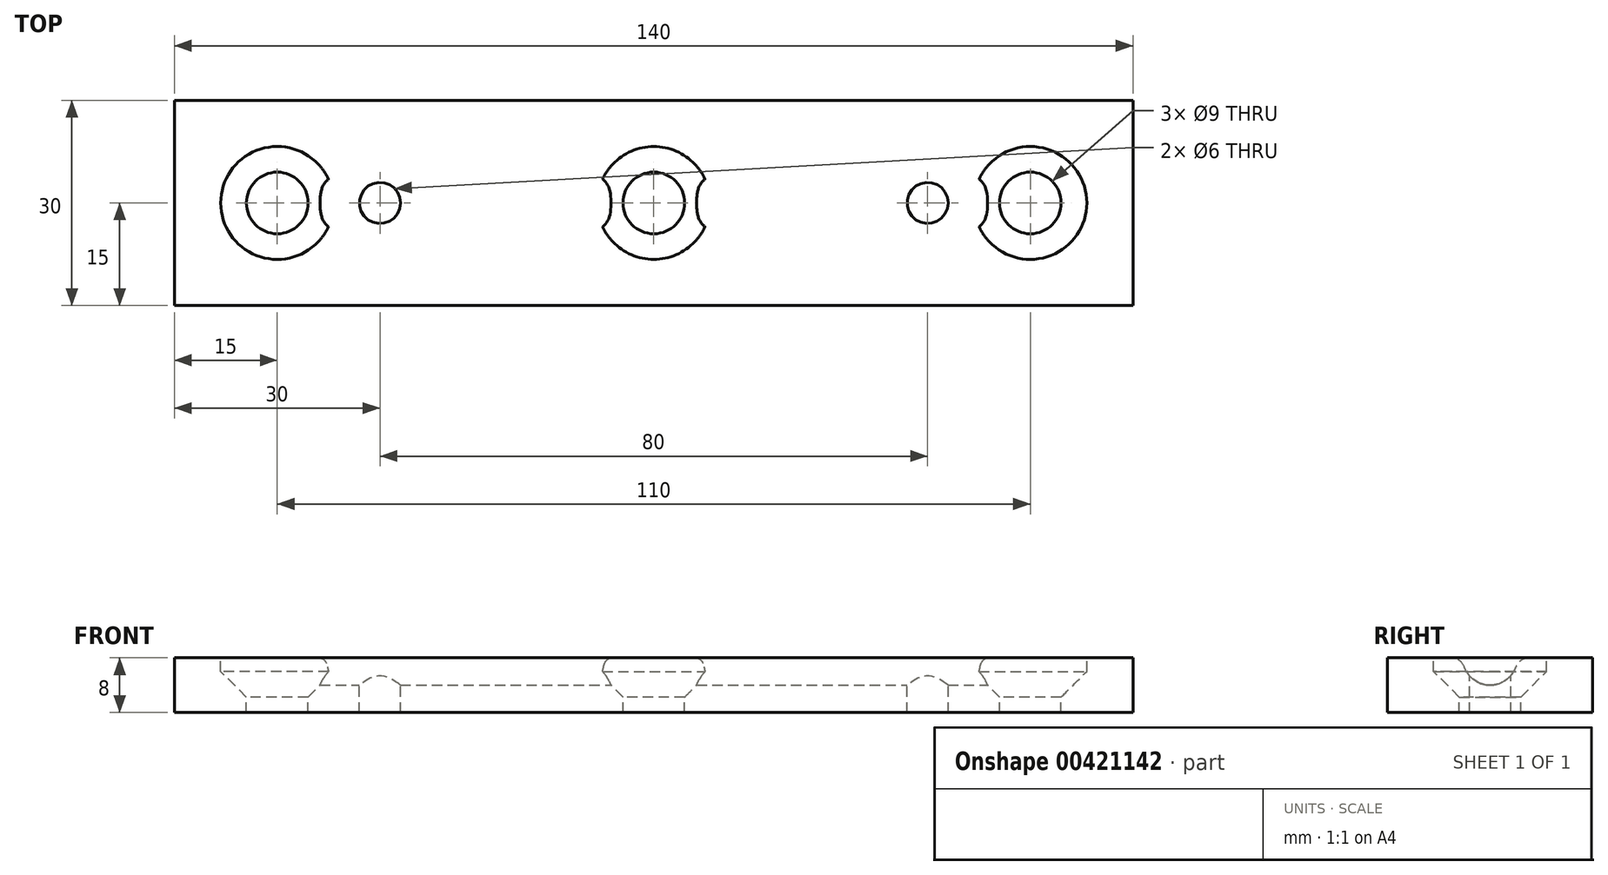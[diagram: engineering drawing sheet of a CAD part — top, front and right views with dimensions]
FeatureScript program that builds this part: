
annotation { "Feature Type Name" : "Feature", "Feature Type Description" : "" }
export const myFeature = defineFeature(function(context is Context, id is Id, definition is map)
    precondition{}
    {
        {
            var Q0;
            Q0=qCreatedBy(makeId("Top.planeOp"),FACE);
            var sketch = newSketch(context, id + "F0", { "sketchPlane" : qUnion([Q0])});
            skLineSegment(sketch, "E0.bottom", {"start": v(-70, 15) * mm, "end": v(70, 15) * mm});
            skLineSegment(sketch, "E0.top", {"start": v(-70, -15) * mm, "end": v(70, -15) * mm});
            skLineSegment(sketch, "E0.left", {"start": v(-70, 15) * mm, "end": v(-70, -15) * mm});
            skLineSegment(sketch, "E0.right", {"start": v(70, 15) * mm, "end": v(70, -15) * mm});
            skPoint(sketch, "E0.middle", {"position": v(0, 0) * mm});
            skSolve(sketch);
        }
        {
            var Q0;
            Q0=qSketchRegion(id+"F0",true);
            extrude(context, id + "F1", {"entities" : qUnion([Q0]), "depth" : 8 * mm});
        }
        {
            var Q0;
            Q0=makeQuery(id+"F1.opExtrude","CAP_FACE",FACE,{"disambiguationData":[OSD([sQuery(id+"F0.wireOp",EDGE,"E0.bottom"),sQuery(id+"F0.wireOp",EDGE,"E0.top"),sQuery(id+"F0.wireOp",EDGE,"E0.left"),sQuery(id+"F0.wireOp",EDGE,"E0.right")])],"isStart":false});
            var sketch = newSketch(context, id + "F2", { "sketchPlane" : qUnion([Q0])});
            skLineSegment(sketch, "E1", {"start": v(-92.77, 0) * mm, "end": v(91.66, 0) * mm, "construction": true});
            skLineSegment(sketch, "E2", {"start": v(0, 45.33) * mm, "end": v(0, -31.87) * mm, "construction": true});
            skPoint(sketch, "E2.endSnap0", {"position": v(0, -15) * mm});
            skLineSegment(sketch, "E3.0", {"start": v(-55, 45.33) * mm, "end": v(-55, -31.87) * mm, "construction": true});
            skCircle(sketch, "E4", {"center": v(-55, 0) * mm, "radius": 8.25 * mm});
            skCircle(sketch, "E5.1.0.0", {"center": v(0, 0) * mm, "radius": 8.25 * mm});
            skCircle(sketch, "E5.2.0.0", {"center": v(55, 0) * mm, "radius": 8.25 * mm});
            skLineSegment(sketch, "E5.direction1", {"start": v(-55, 0) * mm, "end": v(0, 0) * mm, "construction": true});
            skSolve(sketch);
        }
        {
            var Q0;
            Q0=qSketchRegion(id+"F2",true);
            extrude(context, id + "F3", {"entities" : qUnion([Q0]), "operationType" : NewBodyOperationType.REMOVE, "oppositeDirection" : true, "depth" : 2 * mm});
        }
        {
            var Q0;
            Q0=makeQuery(id+"F3.boolean.opBoolean","COPY",FACE,{"derivedFrom":makeQuery(id+"F3.opExtrude","CAP_FACE",FACE,{"disambiguationData":[OSD([sQuery(id+"F2.wireOp",EDGE,"E4")])],"isStart":false})});
            var sketch = newSketch(context, id + "F4", { "sketchPlane" : qUnion([Q0])});
            skCircle(sketch, "E6.0", {"center": v(-55, 0) * mm, "radius": 8.25 * mm, "construction": true});
            skPoint(sketch, "E7.1.0.0", {"position": v(0, 0) * mm});
            skPoint(sketch, "E7.2.0.0", {"position": v(55, 0) * mm});
            skLineSegment(sketch, "E7.direction1", {"start": v(-55, 0) * mm, "end": v(0, 0) * mm, "construction": true});
            skSolve(sketch);
        }
        {
            var Q0;
            Q0=sQuery(id+"F4.wireOp",VERTEX,"E6.0.center");
            var Q1;
            Q1=sQuery(id+"F4.wireOp",VERTEX,"E7.1.0.0");
            var Q2;
            Q2=sQuery(id+"F4.wireOp",VERTEX,"E7.2.0.0");
            var Q3;
            Q3=makeQuery(id+"F1.opExtrude","SWEPT_BODY",BODY,{"disambiguationData":[OSD([sQuery(id+"F0.wireOp",EDGE,"E0.bottom"),sQuery(id+"F0.wireOp",EDGE,"E0.top"),sQuery(id+"F0.wireOp",EDGE,"E0.left"),sQuery(id+"F0.wireOp",EDGE,"E0.right")])]});
            hole(context, id + "F5", {"style" : HoleStyle.C_SINK, "endStyle" : HoleEndStyle.THROUGH, "standardTappedOrClearance" : lookupTablePath({ "standard" : "ISO", "size" : "9", "type" : "Drilled" }), "standardBlindInLast" : lookupTablePath({ "standard" : "ISO", "size" : "9", "type" : "Drilled" }), "holeDiameter" : 9 * mm, "cSinkDiameter" : 16.5 * mm, "cSinkAngle" : 90 * degree, "locations" : qUnion([Q0, Q1, Q2]), "scope" : qUnion([Q3]), "isTappedThrough" : true});
        }
        {
            var Q0;
            Q0=qCreatedBy(makeId("Right.planeOp"),FACE);
            var sketch = newSketch(context, id + "F6", { "sketchPlane" : qUnion([Q0])});
            skLineSegment(sketch, "E8.0.0", {"start": v(15, 8) * mm, "end": v(-15, 8) * mm, "construction": true});
            skLineSegment(sketch, "E8.0.2", {"start": v(-15, 8) * mm, "end": v(15, 8) * mm, "construction": true});
            skCircle(sketch, "E9", {"center": v(0, 8) * mm, "radius": 4 * mm});
            skSolve(sketch);
        }
        {
            var Q0;
            Q0=qSketchRegion(id+"F6",true);
            extrude(context, id + "F7", {"entities" : qUnion([Q0]), "operationType" : NewBodyOperationType.REMOVE, "endBound" : BoundingType.SYMMETRIC, "oppositeDirection" : true, "depth" : 110 * mm});
        }
        {
            var Q0;
            Q0=makeQuery(id+"F7.boolean.opBoolean","INTERSECT",EDGE,{"disambiguationData":[OD(1.0)],"derivedFrom":[makeQuery(id+"F1.opExtrude","CAP_FACE",FACE,{"disambiguationData":[OSD([sQuery(id+"F0.wireOp",EDGE,"E0.bottom"),sQuery(id+"F0.wireOp",EDGE,"E0.top"),sQuery(id+"F0.wireOp",EDGE,"E0.left"),sQuery(id+"F0.wireOp",EDGE,"E0.right")])],"isStart":false}),makeQuery(id+"F7.opExtrude","SWEPT_FACE",FACE,{"disambiguationData":[OSD([sQuery(id+"F6.wireOp",EDGE,"E9")])]})]});
            var Q1;
            Q1=makeQuery(id+"F7.boolean.opBoolean","INTERSECT",EDGE,{"disambiguationData":[OD(3.0)],"derivedFrom":[makeQuery(id+"F1.opExtrude","CAP_FACE",FACE,{"disambiguationData":[OSD([sQuery(id+"F0.wireOp",EDGE,"E0.bottom"),sQuery(id+"F0.wireOp",EDGE,"E0.top"),sQuery(id+"F0.wireOp",EDGE,"E0.left"),sQuery(id+"F0.wireOp",EDGE,"E0.right")])],"isStart":false}),makeQuery(id+"F7.opExtrude","SWEPT_FACE",FACE,{"disambiguationData":[OSD([sQuery(id+"F6.wireOp",EDGE,"E9")])]})]});
            var Q2;
            Q2=makeQuery(id+"F7.boolean.opBoolean","INTERSECT",EDGE,{"disambiguationData":[OD(0.0)],"derivedFrom":[makeQuery(id+"F1.opExtrude","CAP_FACE",FACE,{"disambiguationData":[OSD([sQuery(id+"F0.wireOp",EDGE,"E0.bottom"),sQuery(id+"F0.wireOp",EDGE,"E0.top"),sQuery(id+"F0.wireOp",EDGE,"E0.left"),sQuery(id+"F0.wireOp",EDGE,"E0.right")])],"isStart":false}),makeQuery(id+"F7.opExtrude","SWEPT_FACE",FACE,{"disambiguationData":[OSD([sQuery(id+"F6.wireOp",EDGE,"E9")])]})]});
            var Q3;
            Q3=makeQuery(id+"F7.boolean.opBoolean","INTERSECT",EDGE,{"disambiguationData":[OD(2.0)],"derivedFrom":[makeQuery(id+"F1.opExtrude","CAP_FACE",FACE,{"disambiguationData":[OSD([sQuery(id+"F0.wireOp",EDGE,"E0.bottom"),sQuery(id+"F0.wireOp",EDGE,"E0.top"),sQuery(id+"F0.wireOp",EDGE,"E0.left"),sQuery(id+"F0.wireOp",EDGE,"E0.right")])],"isStart":false}),makeQuery(id+"F7.opExtrude","SWEPT_FACE",FACE,{"disambiguationData":[OSD([sQuery(id+"F6.wireOp",EDGE,"E9")])]})]});
            fillet(context, id + "F8", {"entities" : qUnion([Q0, Q1, Q2, Q3]), "radius" : 2 * mm, "tangentPropagation" : true, "allowEdgeOverflow" : false});
        }
        {
            var Q0;
            Q0=makeQuery(id+"F1.opExtrude","CAP_FACE",FACE,{"disambiguationData":[OSD([sQuery(id+"F0.wireOp",EDGE,"E0.bottom"),sQuery(id+"F0.wireOp",EDGE,"E0.top"),sQuery(id+"F0.wireOp",EDGE,"E0.left"),sQuery(id+"F0.wireOp",EDGE,"E0.right")])],"isStart":false});
            var sketch = newSketch(context, id + "F9", { "sketchPlane" : qUnion([Q0])});
            skLineSegment(sketch, "E10", {"start": v(0, 35.15) * mm, "end": v(0, -22.87) * mm, "construction": true});
            skLineSegment(sketch, "E11", {"start": v(-80.6, 0) * mm, "end": v(81.16, 0) * mm, "construction": true});
            skPoint(sketch, "E11.startSnap0", {"position": v(-63.25, 0) * mm});
            skLineSegment(sketch, "E12.0", {"start": v(-40, 35.15) * mm, "end": v(-40, -22.87) * mm, "construction": true});
            skPoint(sketch, "E13", {"position": v(-40, 0) * mm});
            skPoint(sketch, "E14.MirrorP", {"position": v(40, 0) * mm});
            skSolve(sketch);
        }
        {
            var Q0;
            Q0=sQuery(id+"F9.wireOp",VERTEX,"E13");
            var Q1;
            Q1=sQuery(id+"F9.wireOp",VERTEX,"E14.MirrorP");
            var Q2;
            Q2=makeQuery(id+"F1.opExtrude","SWEPT_BODY",BODY,{"disambiguationData":[OSD([sQuery(id+"F0.wireOp",EDGE,"E0.bottom"),sQuery(id+"F0.wireOp",EDGE,"E0.top"),sQuery(id+"F0.wireOp",EDGE,"E0.left"),sQuery(id+"F0.wireOp",EDGE,"E0.right")])]});
            hole(context, id + "F10", {"style" : HoleStyle.SIMPLE, "endStyle" : HoleEndStyle.THROUGH, "standardTappedOrClearance" : lookupTablePath({ "standard" : "ISO", "size" : "6", "type" : "Drilled" }), "standardBlindInLast" : lookupTablePath({ "standard" : "ISO", "size" : "6", "type" : "Drilled" }), "holeDiameter" : 6 * mm, "locations" : qUnion([Q0, Q1]), "scope" : qUnion([Q2]), "isTappedThrough" : true});
        }
    });
